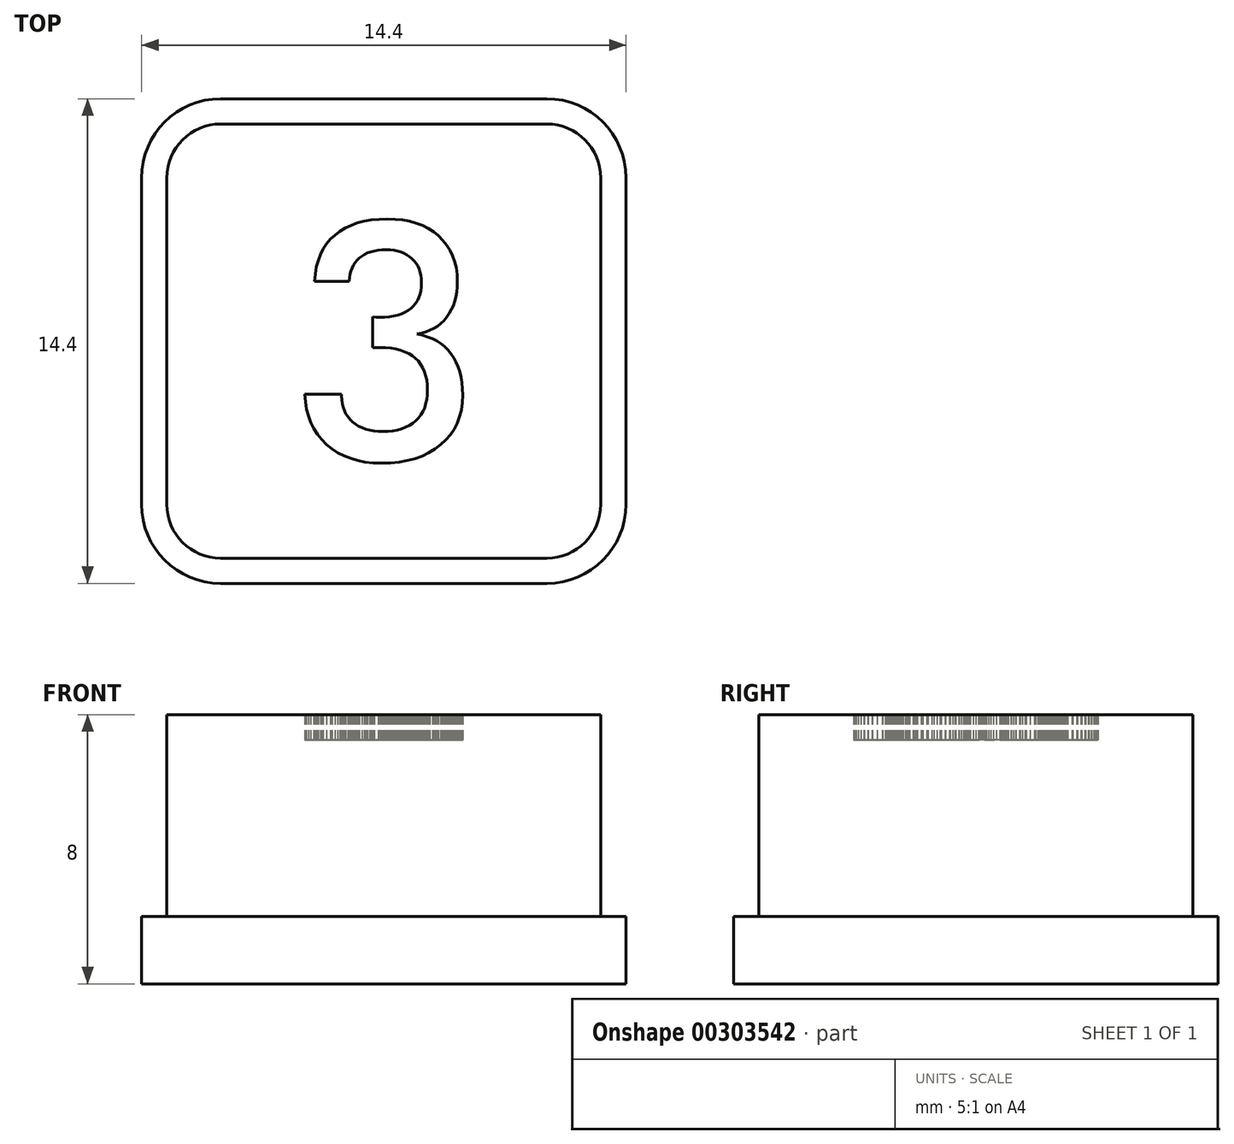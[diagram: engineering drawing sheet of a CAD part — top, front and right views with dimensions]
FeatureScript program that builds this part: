
annotation { "Feature Type Name" : "Feature", "Feature Type Description" : "" }
export const myFeature = defineFeature(function(context is Context, id is Id, definition is map)
    precondition{}
    {
        {
            var Q0;
            Q0=qCreatedBy(makeId("Top.planeOp"),FACE);
            var sketch = newSketch(context, id + "F0", { "sketchPlane" : qUnion([Q0])});
            skArc(sketch, "E0", {"start": v(4.85, -6.45) * mm, "mid": v(5.98, -5.98) * mm, "end": v(6.45, -4.85) * mm});
            skLineSegment(sketch, "E1", {"start": v(6.45, -4.85) * mm, "end": v(6.45, 4.85) * mm});
            skArc(sketch, "E2", {"start": v(6.45, 4.85) * mm, "mid": v(5.98, 5.98) * mm, "end": v(4.85, 6.45) * mm});
            skLineSegment(sketch, "E3", {"start": v(4.85, 6.45) * mm, "end": v(-4.85, 6.45) * mm});
            skArc(sketch, "E4", {"start": v(-4.85, 6.45) * mm, "mid": v(-5.98, 5.98) * mm, "end": v(-6.45, 4.85) * mm});
            skLineSegment(sketch, "E5", {"start": v(-6.45, 4.85) * mm, "end": v(-6.45, -4.85) * mm});
            skArc(sketch, "E6", {"start": v(-6.45, -4.85) * mm, "mid": v(-5.98, -5.98) * mm, "end": v(-4.85, -6.45) * mm});
            skLineSegment(sketch, "E7", {"start": v(-4.85, -6.45) * mm, "end": v(4.85, -6.45) * mm});
            skArc(sketch, "E8", {"start": v(-4.85, 7.2) * mm, "mid": v(-6.51, 6.51) * mm, "end": v(-7.2, 4.85) * mm});
            skLineSegment(sketch, "E9", {"start": v(-7.2, 4.85) * mm, "end": v(-7.2, -4.85) * mm});
            skArc(sketch, "E10", {"start": v(-7.2, -4.85) * mm, "mid": v(-6.51, -6.51) * mm, "end": v(-4.85, -7.2) * mm});
            skLineSegment(sketch, "E11", {"start": v(-4.85, -7.2) * mm, "end": v(4.85, -7.2) * mm});
            skArc(sketch, "E12", {"start": v(4.85, -7.2) * mm, "mid": v(6.51, -6.51) * mm, "end": v(7.2, -4.85) * mm});
            skLineSegment(sketch, "E13", {"start": v(7.2, -4.85) * mm, "end": v(7.2, 4.85) * mm});
            skArc(sketch, "E14", {"start": v(7.2, 4.85) * mm, "mid": v(6.51, 6.51) * mm, "end": v(4.85, 7.2) * mm});
            skLineSegment(sketch, "E15", {"start": v(4.85, 7.2) * mm, "end": v(-4.85, 7.2) * mm});
            skLineSegment(sketch, "E16", {"start": v(-2.35, -1.57) * mm, "end": v(-1.26, -1.57) * mm});
            skLineSegment(sketch, "E17", {"start": v(-1.26, -1.57) * mm, "end": v(-1.26, -1.63) * mm});
            skLineSegment(sketch, "E18", {"start": v(-1.26, -1.63) * mm, "end": v(-1.25, -1.75) * mm});
            skLineSegment(sketch, "E19", {"start": v(-1.25, -1.75) * mm, "end": v(-1.23, -1.86) * mm});
            skLineSegment(sketch, "E20", {"start": v(-1.23, -1.86) * mm, "end": v(-1.2, -1.97) * mm});
            skLineSegment(sketch, "E21", {"start": v(-1.2, -1.97) * mm, "end": v(-1.17, -2.06) * mm});
            skLineSegment(sketch, "E22", {"start": v(-1.17, -2.06) * mm, "end": v(-1.13, -2.16) * mm});
            skLineSegment(sketch, "E23", {"start": v(-1.13, -2.16) * mm, "end": v(-1.07, -2.24) * mm});
            skLineSegment(sketch, "E24", {"start": v(-1.07, -2.24) * mm, "end": v(-1, -2.33) * mm});
            skLineSegment(sketch, "E25", {"start": v(-1, -2.33) * mm, "end": v(-0.93, -2.4) * mm});
            skLineSegment(sketch, "E26", {"start": v(-0.93, -2.4) * mm, "end": v(-0.84, -2.47) * mm});
            skLineSegment(sketch, "E27", {"start": v(-0.84, -2.47) * mm, "end": v(-0.75, -2.53) * mm});
            skLineSegment(sketch, "E28", {"start": v(-0.75, -2.53) * mm, "end": v(-0.64, -2.58) * mm});
            skLineSegment(sketch, "E29", {"start": v(-0.64, -2.58) * mm, "end": v(-0.54, -2.62) * mm});
            skLineSegment(sketch, "E30", {"start": v(-0.54, -2.62) * mm, "end": v(-0.42, -2.65) * mm});
            skLineSegment(sketch, "E31", {"start": v(-0.42, -2.65) * mm, "end": v(-0.3, -2.67) * mm});
            skLineSegment(sketch, "E32", {"start": v(-0.3, -2.67) * mm, "end": v(-0.17, -2.68) * mm});
            skLineSegment(sketch, "E33", {"start": v(-0.17, -2.68) * mm, "end": v(-0.03, -2.69) * mm});
            skLineSegment(sketch, "E34", {"start": v(-0.03, -2.69) * mm, "end": v(0.12, -2.68) * mm});
            skLineSegment(sketch, "E35", {"start": v(0.12, -2.68) * mm, "end": v(0.27, -2.67) * mm});
            skLineSegment(sketch, "E36", {"start": v(0.27, -2.67) * mm, "end": v(0.4, -2.64) * mm});
            skLineSegment(sketch, "E37", {"start": v(0.4, -2.64) * mm, "end": v(0.53, -2.6) * mm});
            skLineSegment(sketch, "E38", {"start": v(0.53, -2.6) * mm, "end": v(0.65, -2.56) * mm});
            skLineSegment(sketch, "E39", {"start": v(0.65, -2.56) * mm, "end": v(0.76, -2.5) * mm});
            skLineSegment(sketch, "E40", {"start": v(0.76, -2.5) * mm, "end": v(0.86, -2.44) * mm});
            skLineSegment(sketch, "E41", {"start": v(0.86, -2.44) * mm, "end": v(0.95, -2.37) * mm});
            skLineSegment(sketch, "E42", {"start": v(0.95, -2.37) * mm, "end": v(1.03, -2.29) * mm});
            skLineSegment(sketch, "E43", {"start": v(1.03, -2.29) * mm, "end": v(1.1, -2.2) * mm});
            skLineSegment(sketch, "E44", {"start": v(1.1, -2.2) * mm, "end": v(1.16, -2.1) * mm});
            skLineSegment(sketch, "E45", {"start": v(1.16, -2.1) * mm, "end": v(1.21, -1.98) * mm});
            skLineSegment(sketch, "E46", {"start": v(1.21, -1.98) * mm, "end": v(1.25, -1.86) * mm});
            skLineSegment(sketch, "E47", {"start": v(1.25, -1.86) * mm, "end": v(1.28, -1.73) * mm});
            skLineSegment(sketch, "E48", {"start": v(1.28, -1.73) * mm, "end": v(1.3, -1.6) * mm});
            skLineSegment(sketch, "E49", {"start": v(1.3, -1.6) * mm, "end": v(1.3, -1.45) * mm});
            skLineSegment(sketch, "E50", {"start": v(1.3, -1.45) * mm, "end": v(1.3, -1.3) * mm});
            skLineSegment(sketch, "E51", {"start": v(1.3, -1.3) * mm, "end": v(1.28, -1.16) * mm});
            skLineSegment(sketch, "E52", {"start": v(1.28, -1.16) * mm, "end": v(1.25, -1.03) * mm});
            skLineSegment(sketch, "E53", {"start": v(1.25, -1.03) * mm, "end": v(1.2, -0.9) * mm});
            skLineSegment(sketch, "E54", {"start": v(1.2, -0.9) * mm, "end": v(1.16, -0.8) * mm});
            skLineSegment(sketch, "E55", {"start": v(1.16, -0.8) * mm, "end": v(1.1, -0.69) * mm});
            skLineSegment(sketch, "E56", {"start": v(1.1, -0.69) * mm, "end": v(1.03, -0.6) * mm});
            skLineSegment(sketch, "E57", {"start": v(1.03, -0.6) * mm, "end": v(0.94, -0.5) * mm});
            skLineSegment(sketch, "E58", {"start": v(0.94, -0.5) * mm, "end": v(0.85, -0.43) * mm});
            skLineSegment(sketch, "E59", {"start": v(0.85, -0.43) * mm, "end": v(0.74, -0.37) * mm});
            skLineSegment(sketch, "E60", {"start": v(0.74, -0.37) * mm, "end": v(0.63, -0.32) * mm});
            skLineSegment(sketch, "E61", {"start": v(0.63, -0.32) * mm, "end": v(0.5, -0.27) * mm});
            skLineSegment(sketch, "E62", {"start": v(0.5, -0.27) * mm, "end": v(0.36, -0.24) * mm});
            skLineSegment(sketch, "E63", {"start": v(0.36, -0.24) * mm, "end": v(0.2, -0.21) * mm});
            skLineSegment(sketch, "E64", {"start": v(0.2, -0.21) * mm, "end": v(0.05, -0.2) * mm});
            skLineSegment(sketch, "E65", {"start": v(0.05, -0.2) * mm, "end": v(-0.12, -0.2) * mm});
            skLineSegment(sketch, "E66", {"start": v(-0.12, -0.2) * mm, "end": v(-0.23, -0.2) * mm});
            skLineSegment(sketch, "E67", {"start": v(-0.23, -0.2) * mm, "end": v(-0.34, -0.2) * mm});
            skLineSegment(sketch, "E68", {"start": v(-0.34, -0.2) * mm, "end": v(-0.34, 0.72) * mm});
            skLineSegment(sketch, "E69", {"start": v(-0.34, 0.72) * mm, "end": v(-0.23, 0.71) * mm});
            skLineSegment(sketch, "E70", {"start": v(-0.23, 0.71) * mm, "end": v(-0.13, 0.7) * mm});
            skLineSegment(sketch, "E71", {"start": v(-0.13, 0.7) * mm, "end": v(0.02, 0.71) * mm});
            skLineSegment(sketch, "E72", {"start": v(0.02, 0.71) * mm, "end": v(0.16, 0.72) * mm});
            skLineSegment(sketch, "E73", {"start": v(0.16, 0.72) * mm, "end": v(0.3, 0.74) * mm});
            skLineSegment(sketch, "E74", {"start": v(0.3, 0.74) * mm, "end": v(0.41, 0.77) * mm});
            skLineSegment(sketch, "E75", {"start": v(0.41, 0.77) * mm, "end": v(0.53, 0.8) * mm});
            skLineSegment(sketch, "E76", {"start": v(0.53, 0.8) * mm, "end": v(0.63, 0.85) * mm});
            skLineSegment(sketch, "E77", {"start": v(0.63, 0.85) * mm, "end": v(0.72, 0.9) * mm});
            skLineSegment(sketch, "E78", {"start": v(0.72, 0.9) * mm, "end": v(0.8, 0.97) * mm});
            skLineSegment(sketch, "E79", {"start": v(0.8, 0.97) * mm, "end": v(0.88, 1.04) * mm});
            skLineSegment(sketch, "E80", {"start": v(0.88, 1.04) * mm, "end": v(0.94, 1.11) * mm});
            skLineSegment(sketch, "E81", {"start": v(0.94, 1.11) * mm, "end": v(1, 1.2) * mm});
            skLineSegment(sketch, "E82", {"start": v(1, 1.2) * mm, "end": v(1.04, 1.3) * mm});
            skLineSegment(sketch, "E83", {"start": v(1.04, 1.3) * mm, "end": v(1.08, 1.4) * mm});
            skLineSegment(sketch, "E84", {"start": v(1.08, 1.4) * mm, "end": v(1.1, 1.5) * mm});
            skLineSegment(sketch, "E85", {"start": v(1.1, 1.5) * mm, "end": v(1.12, 1.61) * mm});
            skLineSegment(sketch, "E86", {"start": v(1.12, 1.61) * mm, "end": v(1.12, 1.74) * mm});
            skLineSegment(sketch, "E87", {"start": v(1.12, 1.74) * mm, "end": v(1.12, 1.85) * mm});
            skLineSegment(sketch, "E88", {"start": v(1.12, 1.85) * mm, "end": v(1.1, 1.95) * mm});
            skLineSegment(sketch, "E89", {"start": v(1.1, 1.95) * mm, "end": v(1.08, 2.05) * mm});
            skLineSegment(sketch, "E90", {"start": v(1.08, 2.05) * mm, "end": v(1.05, 2.14) * mm});
            skLineSegment(sketch, "E91", {"start": v(1.05, 2.14) * mm, "end": v(1.01, 2.23) * mm});
            skLineSegment(sketch, "E92", {"start": v(1.01, 2.23) * mm, "end": v(0.96, 2.3) * mm});
            skLineSegment(sketch, "E93", {"start": v(0.96, 2.3) * mm, "end": v(0.9, 2.38) * mm});
            skLineSegment(sketch, "E94", {"start": v(0.9, 2.38) * mm, "end": v(0.84, 2.45) * mm});
            skLineSegment(sketch, "E95", {"start": v(0.84, 2.45) * mm, "end": v(0.76, 2.51) * mm});
            skLineSegment(sketch, "E96", {"start": v(0.76, 2.51) * mm, "end": v(0.68, 2.57) * mm});
            skLineSegment(sketch, "E97", {"start": v(0.68, 2.57) * mm, "end": v(0.6, 2.61) * mm});
            skLineSegment(sketch, "E98", {"start": v(0.6, 2.61) * mm, "end": v(0.5, 2.65) * mm});
            skLineSegment(sketch, "E99", {"start": v(0.5, 2.65) * mm, "end": v(0.4, 2.68) * mm});
            skLineSegment(sketch, "E100", {"start": v(0.4, 2.68) * mm, "end": v(0.3, 2.7) * mm});
            skLineSegment(sketch, "E101", {"start": v(0.3, 2.7) * mm, "end": v(0.2, 2.71) * mm});
            skLineSegment(sketch, "E102", {"start": v(0.2, 2.71) * mm, "end": v(0.07, 2.72) * mm});
            skLineSegment(sketch, "E103", {"start": v(0.07, 2.72) * mm, "end": v(-0.05, 2.71) * mm});
            skLineSegment(sketch, "E104", {"start": v(-0.05, 2.71) * mm, "end": v(-0.17, 2.7) * mm});
            skLineSegment(sketch, "E105", {"start": v(-0.17, 2.7) * mm, "end": v(-0.28, 2.68) * mm});
            skLineSegment(sketch, "E106", {"start": v(-0.28, 2.68) * mm, "end": v(-0.38, 2.65) * mm});
            skLineSegment(sketch, "E107", {"start": v(-0.38, 2.65) * mm, "end": v(-0.48, 2.62) * mm});
            skLineSegment(sketch, "E108", {"start": v(-0.48, 2.62) * mm, "end": v(-0.57, 2.58) * mm});
            skLineSegment(sketch, "E109", {"start": v(-0.57, 2.58) * mm, "end": v(-0.65, 2.53) * mm});
            skLineSegment(sketch, "E110", {"start": v(-0.65, 2.53) * mm, "end": v(-0.73, 2.47) * mm});
            skLineSegment(sketch, "E111", {"start": v(-0.73, 2.47) * mm, "end": v(-0.8, 2.4) * mm});
            skLineSegment(sketch, "E112", {"start": v(-0.8, 2.4) * mm, "end": v(-0.85, 2.33) * mm});
            skLineSegment(sketch, "E113", {"start": v(-0.85, 2.33) * mm, "end": v(-0.9, 2.26) * mm});
            skLineSegment(sketch, "E114", {"start": v(-0.9, 2.26) * mm, "end": v(-0.95, 2.17) * mm});
            skLineSegment(sketch, "E115", {"start": v(-0.95, 2.17) * mm, "end": v(-0.98, 2.08) * mm});
            skLineSegment(sketch, "E116", {"start": v(-0.98, 2.08) * mm, "end": v(-1, 1.99) * mm});
            skLineSegment(sketch, "E117", {"start": v(-1, 1.99) * mm, "end": v(-1.02, 1.89) * mm});
            skLineSegment(sketch, "E118", {"start": v(-1.02, 1.89) * mm, "end": v(-1.03, 1.78) * mm});
            skLineSegment(sketch, "E119", {"start": v(-1.03, 1.78) * mm, "end": v(-2.06, 1.78) * mm});
            skLineSegment(sketch, "E120", {"start": v(-2.06, 1.78) * mm, "end": v(-2.04, 2) * mm});
            skLineSegment(sketch, "E121", {"start": v(-2.04, 2) * mm, "end": v(-2, 2.2) * mm});
            skLineSegment(sketch, "E122", {"start": v(-2, 2.2) * mm, "end": v(-1.95, 2.4) * mm});
            skLineSegment(sketch, "E123", {"start": v(-1.95, 2.4) * mm, "end": v(-1.88, 2.57) * mm});
            skLineSegment(sketch, "E124", {"start": v(-1.88, 2.57) * mm, "end": v(-1.8, 2.73) * mm});
            skLineSegment(sketch, "E125", {"start": v(-1.8, 2.73) * mm, "end": v(-1.7, 2.89) * mm});
            skLineSegment(sketch, "E126", {"start": v(-1.7, 2.89) * mm, "end": v(-1.58, 3.02) * mm});
            skLineSegment(sketch, "E127", {"start": v(-1.58, 3.02) * mm, "end": v(-1.45, 3.15) * mm});
            skLineSegment(sketch, "E128", {"start": v(-1.45, 3.15) * mm, "end": v(-1.3, 3.26) * mm});
            skLineSegment(sketch, "E129", {"start": v(-1.3, 3.26) * mm, "end": v(-1.14, 3.36) * mm});
            skLineSegment(sketch, "E130", {"start": v(-1.14, 3.36) * mm, "end": v(-0.97, 3.44) * mm});
            skLineSegment(sketch, "E131", {"start": v(-0.97, 3.44) * mm, "end": v(-0.78, 3.5) * mm});
            skLineSegment(sketch, "E132", {"start": v(-0.78, 3.5) * mm, "end": v(-0.58, 3.56) * mm});
            skLineSegment(sketch, "E133", {"start": v(-0.58, 3.56) * mm, "end": v(-0.37, 3.6) * mm});
            skLineSegment(sketch, "E134", {"start": v(-0.37, 3.6) * mm, "end": v(-0.14, 3.62) * mm});
            skLineSegment(sketch, "E135", {"start": v(-0.14, 3.62) * mm, "end": v(0.1, 3.63) * mm});
            skLineSegment(sketch, "E136", {"start": v(0.1, 3.63) * mm, "end": v(0.34, 3.62) * mm});
            skLineSegment(sketch, "E137", {"start": v(0.34, 3.62) * mm, "end": v(0.56, 3.6) * mm});
            skLineSegment(sketch, "E138", {"start": v(0.56, 3.6) * mm, "end": v(0.77, 3.56) * mm});
            skLineSegment(sketch, "E139", {"start": v(0.77, 3.56) * mm, "end": v(0.96, 3.5) * mm});
            skLineSegment(sketch, "E140", {"start": v(0.96, 3.5) * mm, "end": v(1.15, 3.43) * mm});
            skLineSegment(sketch, "E141", {"start": v(1.15, 3.43) * mm, "end": v(1.32, 3.35) * mm});
            skLineSegment(sketch, "E142", {"start": v(1.32, 3.35) * mm, "end": v(1.48, 3.24) * mm});
            skLineSegment(sketch, "E143", {"start": v(1.48, 3.24) * mm, "end": v(1.63, 3.13) * mm});
            skLineSegment(sketch, "E144", {"start": v(1.63, 3.13) * mm, "end": v(1.76, 3) * mm});
            skLineSegment(sketch, "E145", {"start": v(1.76, 3) * mm, "end": v(1.87, 2.85) * mm});
            skLineSegment(sketch, "E146", {"start": v(1.87, 2.85) * mm, "end": v(1.97, 2.7) * mm});
            skLineSegment(sketch, "E147", {"start": v(1.97, 2.7) * mm, "end": v(2.05, 2.54) * mm});
            skLineSegment(sketch, "E148", {"start": v(2.05, 2.54) * mm, "end": v(2.1, 2.36) * mm});
            skLineSegment(sketch, "E149", {"start": v(2.1, 2.36) * mm, "end": v(2.15, 2.17) * mm});
            skLineSegment(sketch, "E150", {"start": v(2.15, 2.17) * mm, "end": v(2.18, 1.98) * mm});
            skLineSegment(sketch, "E151", {"start": v(2.18, 1.98) * mm, "end": v(2.19, 1.77) * mm});
            skLineSegment(sketch, "E152", {"start": v(2.19, 1.77) * mm, "end": v(2.18, 1.61) * mm});
            skLineSegment(sketch, "E153", {"start": v(2.18, 1.61) * mm, "end": v(2.17, 1.46) * mm});
            skLineSegment(sketch, "E154", {"start": v(2.17, 1.46) * mm, "end": v(2.14, 1.32) * mm});
            skLineSegment(sketch, "E155", {"start": v(2.14, 1.32) * mm, "end": v(2.1, 1.18) * mm});
            skLineSegment(sketch, "E156", {"start": v(2.1, 1.18) * mm, "end": v(2.06, 1.05) * mm});
            skLineSegment(sketch, "E157", {"start": v(2.06, 1.05) * mm, "end": v(2, 0.93) * mm});
            skLineSegment(sketch, "E158", {"start": v(2, 0.93) * mm, "end": v(1.94, 0.82) * mm});
            skLineSegment(sketch, "E159", {"start": v(1.94, 0.82) * mm, "end": v(1.87, 0.71) * mm});
            skLineSegment(sketch, "E160", {"start": v(1.87, 0.71) * mm, "end": v(1.79, 0.61) * mm});
            skLineSegment(sketch, "E161", {"start": v(1.79, 0.61) * mm, "end": v(1.7, 0.52) * mm});
            skLineSegment(sketch, "E162", {"start": v(1.7, 0.52) * mm, "end": v(1.6, 0.45) * mm});
            skLineSegment(sketch, "E163", {"start": v(1.6, 0.45) * mm, "end": v(1.5, 0.38) * mm});
            skLineSegment(sketch, "E164", {"start": v(1.5, 0.38) * mm, "end": v(1.38, 0.32) * mm});
            skLineSegment(sketch, "E165", {"start": v(1.38, 0.32) * mm, "end": v(1.25, 0.27) * mm});
            skLineSegment(sketch, "E166", {"start": v(1.25, 0.27) * mm, "end": v(1.12, 0.24) * mm});
            skLineSegment(sketch, "E167", {"start": v(1.12, 0.24) * mm, "end": v(0.99, 0.21) * mm});
            skLineSegment(sketch, "E168", {"start": v(0.99, 0.21) * mm, "end": v(1.15, 0.18) * mm});
            skLineSegment(sketch, "E169", {"start": v(1.15, 0.18) * mm, "end": v(1.3, 0.13) * mm});
            skLineSegment(sketch, "E170", {"start": v(1.3, 0.13) * mm, "end": v(1.44, 0.07) * mm});
            skLineSegment(sketch, "E171", {"start": v(1.44, 0.07) * mm, "end": v(1.57, 0) * mm});
            skLineSegment(sketch, "E172", {"start": v(1.57, 0) * mm, "end": v(1.7, -0.07) * mm});
            skLineSegment(sketch, "E173", {"start": v(1.7, -0.07) * mm, "end": v(1.8, -0.16) * mm});
            skLineSegment(sketch, "E174", {"start": v(1.8, -0.16) * mm, "end": v(1.9, -0.26) * mm});
            skLineSegment(sketch, "E175", {"start": v(1.9, -0.26) * mm, "end": v(2, -0.37) * mm});
            skLineSegment(sketch, "E176", {"start": v(2, -0.37) * mm, "end": v(2.08, -0.5) * mm});
            skLineSegment(sketch, "E177", {"start": v(2.08, -0.5) * mm, "end": v(2.15, -0.62) * mm});
            skLineSegment(sketch, "E178", {"start": v(2.15, -0.62) * mm, "end": v(2.2, -0.76) * mm});
            skLineSegment(sketch, "E179", {"start": v(2.2, -0.76) * mm, "end": v(2.26, -0.91) * mm});
            skLineSegment(sketch, "E180", {"start": v(2.26, -0.91) * mm, "end": v(2.3, -1.07) * mm});
            skLineSegment(sketch, "E181", {"start": v(2.3, -1.07) * mm, "end": v(2.32, -1.24) * mm});
            skLineSegment(sketch, "E182", {"start": v(2.32, -1.24) * mm, "end": v(2.34, -1.42) * mm});
            skLineSegment(sketch, "E183", {"start": v(2.34, -1.42) * mm, "end": v(2.35, -1.6) * mm});
            skLineSegment(sketch, "E184", {"start": v(2.35, -1.6) * mm, "end": v(2.34, -1.83) * mm});
            skLineSegment(sketch, "E185", {"start": v(2.34, -1.83) * mm, "end": v(2.3, -2.04) * mm});
            skLineSegment(sketch, "E186", {"start": v(2.3, -2.04) * mm, "end": v(2.25, -2.25) * mm});
            skLineSegment(sketch, "E187", {"start": v(2.25, -2.25) * mm, "end": v(2.18, -2.44) * mm});
            skLineSegment(sketch, "E188", {"start": v(2.18, -2.44) * mm, "end": v(2.1, -2.62) * mm});
            skLineSegment(sketch, "E189", {"start": v(2.1, -2.62) * mm, "end": v(1.98, -2.78) * mm});
            skLineSegment(sketch, "E190", {"start": v(1.98, -2.78) * mm, "end": v(1.85, -2.94) * mm});
            skLineSegment(sketch, "E191", {"start": v(1.85, -2.94) * mm, "end": v(1.7, -3.08) * mm});
            skLineSegment(sketch, "E192", {"start": v(1.7, -3.08) * mm, "end": v(1.52, -3.2) * mm});
            skLineSegment(sketch, "E193", {"start": v(1.52, -3.2) * mm, "end": v(1.34, -3.32) * mm});
            skLineSegment(sketch, "E194", {"start": v(1.34, -3.32) * mm, "end": v(1.14, -3.42) * mm});
            skLineSegment(sketch, "E195", {"start": v(1.14, -3.42) * mm, "end": v(0.92, -3.5) * mm});
            skLineSegment(sketch, "E196", {"start": v(0.92, -3.5) * mm, "end": v(0.7, -3.55) * mm});
            skLineSegment(sketch, "E197", {"start": v(0.7, -3.55) * mm, "end": v(0.45, -3.6) * mm});
            skLineSegment(sketch, "E198", {"start": v(0.45, -3.6) * mm, "end": v(0.2, -3.62) * mm});
            skLineSegment(sketch, "E199", {"start": v(0.2, -3.62) * mm, "end": v(-0.07, -3.63) * mm});
            skLineSegment(sketch, "E200", {"start": v(-0.07, -3.63) * mm, "end": v(-0.32, -3.62) * mm});
            skLineSegment(sketch, "E201", {"start": v(-0.32, -3.62) * mm, "end": v(-0.55, -3.6) * mm});
            skLineSegment(sketch, "E202", {"start": v(-0.55, -3.6) * mm, "end": v(-0.78, -3.55) * mm});
            skLineSegment(sketch, "E203", {"start": v(-0.78, -3.55) * mm, "end": v(-0.98, -3.49) * mm});
            skLineSegment(sketch, "E204", {"start": v(-0.98, -3.49) * mm, "end": v(-1.18, -3.41) * mm});
            skLineSegment(sketch, "E205", {"start": v(-1.18, -3.41) * mm, "end": v(-1.37, -3.32) * mm});
            skLineSegment(sketch, "E206", {"start": v(-1.37, -3.32) * mm, "end": v(-1.54, -3.2) * mm});
            skLineSegment(sketch, "E207", {"start": v(-1.54, -3.2) * mm, "end": v(-1.7, -3.07) * mm});
            skLineSegment(sketch, "E208", {"start": v(-1.7, -3.07) * mm, "end": v(-1.84, -2.93) * mm});
            skLineSegment(sketch, "E209", {"start": v(-1.84, -2.93) * mm, "end": v(-1.97, -2.77) * mm});
            skLineSegment(sketch, "E210", {"start": v(-1.97, -2.77) * mm, "end": v(-2.08, -2.6) * mm});
            skLineSegment(sketch, "E211", {"start": v(-2.08, -2.6) * mm, "end": v(-2.17, -2.42) * mm});
            skLineSegment(sketch, "E212", {"start": v(-2.17, -2.42) * mm, "end": v(-2.24, -2.23) * mm});
            skLineSegment(sketch, "E213", {"start": v(-2.24, -2.23) * mm, "end": v(-2.3, -2.02) * mm});
            skLineSegment(sketch, "E214", {"start": v(-2.3, -2.02) * mm, "end": v(-2.33, -1.8) * mm});
            skLineSegment(sketch, "E215", {"start": v(-2.33, -1.8) * mm, "end": v(-2.35, -1.57) * mm});
            skSolve(sketch);
        }
        {
            var Q0;
            Q0=makeQuery(id+"F0.imprint","IMPRINT",FACE,{"disambiguationData":[TD([[makeQuery(id+"F0.imprint","IMPRINT",EDGE,{"derivedFrom":sQuery(id+"F0.wireOp",EDGE,"E0")}),-1.0]])]});
            extrude(context, id + "F1", {"entities" : qUnion([Q0]), "depth" : 2 * mm});
        }
        {
            var Q0;
            Q0=makeQuery(id+"F0.imprint","IMPRINT",FACE,{"disambiguationData":[TD([[makeQuery(id+"F0.imprint","IMPRINT",EDGE,{"derivedFrom":sQuery(id+"F0.wireOp",EDGE,"E0")}),1.0]])]});
            extrude(context, id + "F2", {"entities" : qUnion([Q0]), "operationType" : NewBodyOperationType.ADD, "depth" : 8 * mm});
        }
        {
            var Q0;
            Q0=makeQuery(id+"F0.imprint","IMPRINT",FACE,{"disambiguationData":[TD([[makeQuery(id+"F0.imprint","IMPRINT",EDGE,{"derivedFrom":sQuery(id+"F0.wireOp",EDGE,"E16")}),-1.0]])]});
            extrude(context, id + "F3", {"entities" : qUnion([Q0]), "operationType" : NewBodyOperationType.ADD, "depth" : 7.25 * mm});
        }
    });
